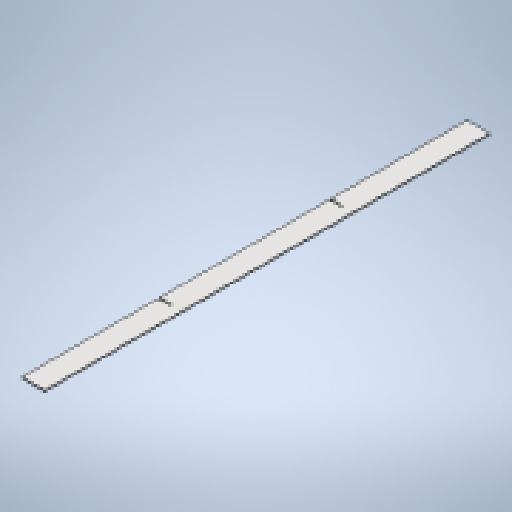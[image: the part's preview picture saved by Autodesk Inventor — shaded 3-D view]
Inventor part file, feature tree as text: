
AUTODESK INVENTOR PART (.ipt)
format: ipt  version: 2025 (Build 290162010, 162A)  size: 214,016 bytes
history: native  units: mm
features: sketch x2, other x2, sheet_metal_op x1, extrude x1, chamfer x1
ambient origin geometry x8: Origin, YZ Plane, XZ Plane, XY Plane, X Axis, Y Axis, Z Axis, Center Point
bodies: Solid1 (feature_tree)
feature tree (7):
  sheet_metal_op  "Face1"
  extrude  "Extrusion1"  Depth=1080.0mm
  chamfer  "Corner Round3"
  sketch  "Sketch1"  dims[d0=50.0mm d1=1080.0mm]
  other  "Plate1"
  sketch  "Sketch2"  dims[d2=3.0mm d15=170.0mm d16=3.0mm d17=26.0mm d18=170.0mm d19=26.0mm d20=3.0mm d21=0.0mm d22=0.0mm d23=3.0mm d24=26.0mm d25=340.0mm d26=26.0mm d27=3.0mm d28=3.0mm d29=340.0mm d30=6.0mm]
  other  "Definition1"
